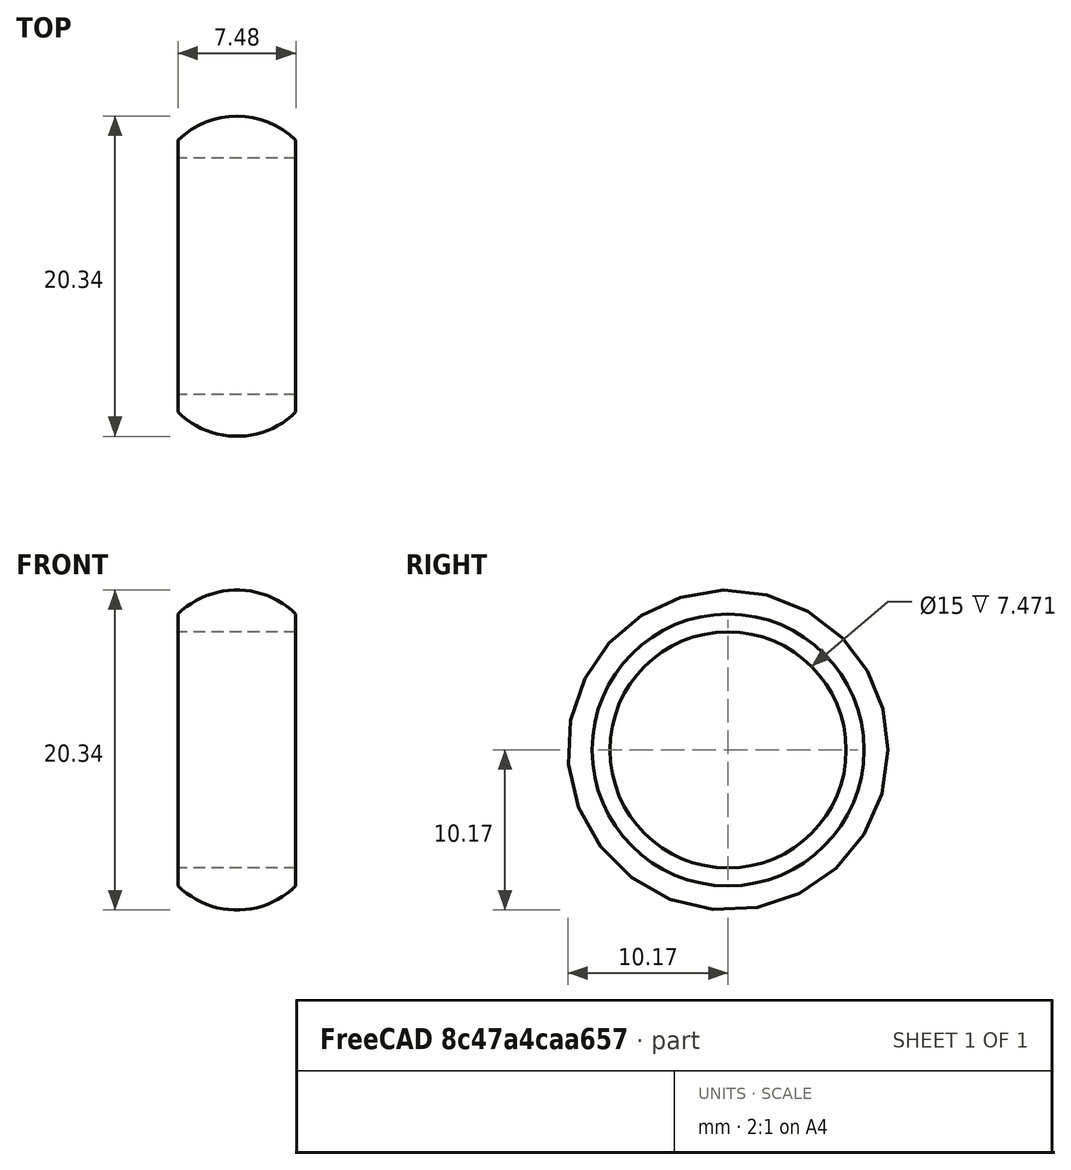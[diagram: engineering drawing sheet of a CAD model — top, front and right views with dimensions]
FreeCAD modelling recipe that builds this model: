
FCSTD DOCUMENT  (FreeCAD 0.16R6705 (Git))
Label: anello
License: All rights reserved
LicenseURL: http://it.wikipedia.org/wiki/<copyright redacted>
objects: Sketcher::SketchObject×1, PartDesign::Revolution×1
note: 3 computed .brp shape members not serialized (recipe doc carries the construction recipe); baked Part::Feature solids carry a one-line shape summary decoded from their .brp

FEATURE [Sketcher::SketchObject] Sketch
  sketch-geometry (4):
    g0: ArcOfCircle CenterX=0 CenterY=4.84318 CenterZ=0 NormalX=0 NormalY=0 NormalZ=1 Radius=5.32229 StartAngle=0.792778 EndAngle=2.34881
    g1: LineSegment StartX=-3.73555 StartY=8.63427 StartZ=0 EndX=-3.73555 EndY=7.5 EndZ=0
    g2: LineSegment StartX=3.73555 StartY=8.63427 StartZ=0 EndX=3.73555 EndY=7.5 EndZ=0
    g3: LineSegment StartX=3.73555 StartY=7.5 StartZ=0 EndX=-3.73555 EndY=7.5 EndZ=0
  constraints (9):
    c: Symmetric(g0,g0,g-2)
    c: Coincident(g1,g3)
    c: Coincident(g3,g2)
    c: Coincident(g0,g2)
    c: Coincident(g0,g1)
    c: Vertical(g1)
    c: Vertical(g2)
    c: Equal(g1,g2)
    c: DistanceY(g-1,g1) = 7.5
FEATURE [PartDesign::Revolution] Revolution
  Angle = 360
  Axis = (1,0,0)
  Base = (0,0,0)
  ReferenceAxis = -> Sketch [H_Axis]
  Sketch = -> Sketch
